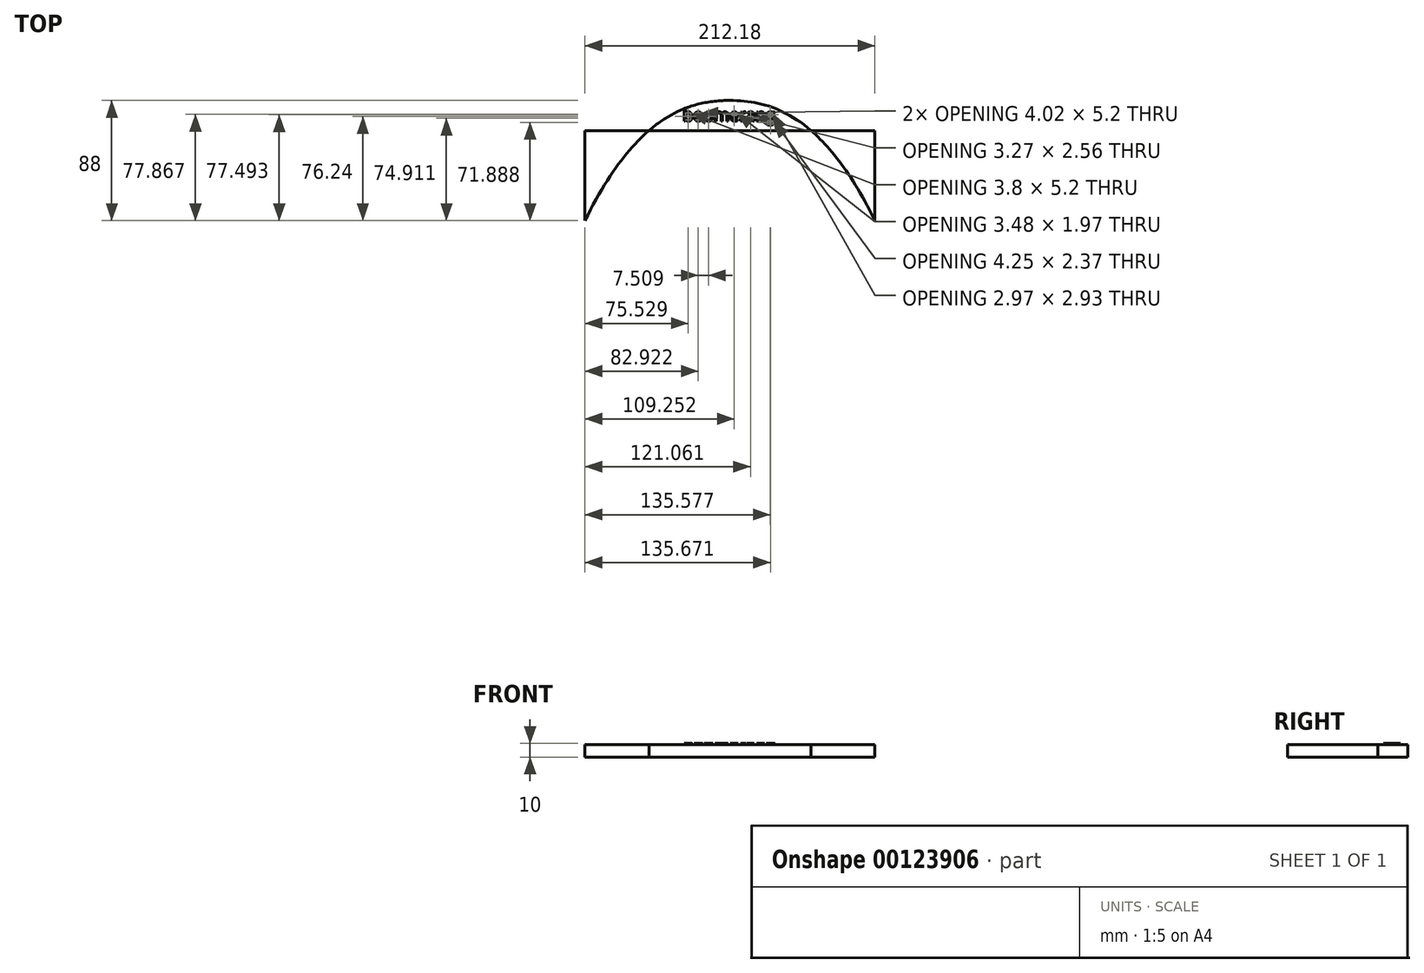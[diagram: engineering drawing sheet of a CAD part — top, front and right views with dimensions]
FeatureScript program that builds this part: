
annotation { "Feature Type Name" : "Feature", "Feature Type Description" : "" }
export const myFeature = defineFeature(function(context is Context, id is Id, definition is map)
    precondition{}
    {
        {
            var Q0;
            Q0=qCreatedBy(makeId("Top.planeOp"),FACE);
            var sketch = newSketch(context, id + "F0", { "sketchPlane" : qUnion([Q0])});
            skLineSegment(sketch, "E0.bottom", {"start": v(-106.09, -33) * mm, "end": v(106.09, -33) * mm});
            skLineSegment(sketch, "E0.top", {"start": v(-106.09, 33) * mm, "end": v(106.09, 33) * mm});
            skLineSegment(sketch, "E0.left", {"start": v(-106.09, -33) * mm, "end": v(-106.09, 33) * mm});
            skLineSegment(sketch, "E0.right", {"start": v(106.09, -33) * mm, "end": v(106.09, 33) * mm});
            skPoint(sketch, "E0.middle", {"position": v(0, 0) * mm});
            skFitSpline(sketch, "E1", {"points": [v(-106.09, -33) * mm, v(0, 33) * mm, v(106.09, -33) * mm], "startDerivative": vector(212.18, 330.16) * mm, "endDerivative": vector(212.18, -330.16) * mm});
            skLineSegment(sketch, "E2", {"start": v(0, 33) * mm, "end": v(0, 55) * mm});
            skFitSpline(sketch, "E3", {"points": [v(-106.09, -33) * mm, v(0, 55) * mm, v(106.09, -33) * mm], "startDerivative": vector(212.18, 430.76) * mm, "endDerivative": vector(212.18, -430.76) * mm});
            skArc(sketch, "E4.filletArc", {"start": v(96.94, -19.72) * mm, "mid": v(98.28, -19.97) * mm, "end": v(98.62, -18.65) * mm});
            skSolve(sketch);
        }
        {
            var Q0;
            {var subQ1=sQuery(id+"F0.wireOp",EDGE,"E0.top");var subQ3=sQuery(id+"F0.wireOp",EDGE,"E3");var subQ4=makeQuery(id+"F0.imprint","INTERSECT",VERTEX,{"disambiguationData":[OD(1.0)],"derivedFrom":[subQ1,subQ3]});Q0=makeQuery(id+"F0.imprint","IMPRINT",FACE,{"disambiguationData":[TD([[makeQuery(id+"F0.imprint","IMPRINT",EDGE,{"disambiguationData":[TD([[subQ4,1.0]])],"derivedFrom":subQ1}),-1.0]])]});}
            var Q1;
            {var subQ1=sQuery(id+"F0.wireOp",EDGE,"E0.top");var subQ3=sQuery(id+"F0.wireOp",EDGE,"E3");var subQ4=makeQuery(id+"F0.imprint","INTERSECT",VERTEX,{"disambiguationData":[OD(0.0)],"derivedFrom":[subQ1,subQ3]});Q1=makeQuery(id+"F0.imprint","IMPRINT",FACE,{"disambiguationData":[TD([[makeQuery(id+"F0.imprint","IMPRINT",EDGE,{"disambiguationData":[TD([[subQ4,-1.0]])],"derivedFrom":subQ1}),-1.0]])]});}
            var Q2;
            {var subQ0=sQuery(id+"F0.wireOp",EDGE,"E2");Q2=makeQuery(id+"F0.imprint","IMPRINT",FACE,{"disambiguationData":[TD([[makeQuery(id+"F0.imprint","IMPRINT",EDGE,{"derivedFrom":subQ0}),-1.0]])]});}
            var Q3;
            {var subQ0=sQuery(id+"F0.wireOp",EDGE,"E2");Q3=makeQuery(id+"F0.imprint","IMPRINT",FACE,{"disambiguationData":[TD([[makeQuery(id+"F0.imprint","IMPRINT",EDGE,{"derivedFrom":subQ0}),1.0]])]});}
            extrude(context, id + "F1", {"entities" : qUnion([Q0, Q1, Q2, Q3]), "depth" : 9 * mm});
        }
        {
            var Q0;
            Q0=makeQuery(id+"F1.opExtrude","CAP_FACE",FACE,{"disambiguationData":[OSD([sQuery(id+"F0.wireOp",EDGE,"E1"),sQuery(id+"F0.wireOp",EDGE,"E3")])],"isStart":false});
            var sketch = newSketch(context, id + "F2", { "sketchPlane" : qUnion([Q0])});
            skText(sketch, "E5", { "text": "boomerang", "fontName": "OpenSans-Regular.ttf"});
            const initialGuessF2  = {"E5": [-0.03454, 0.03992, 1, 0, 0.00895]};
            skSetInitialGuess(sketch, initialGuessF2);
            skSolve(sketch);
        }
        {
            var Q0;
            Q0 = qSketchRegion(id + "F2", true);
            extrude(context, id + "F3", {"entities" : qUnion([Q0]), "depth" : 1 * mm});
        }
    });
